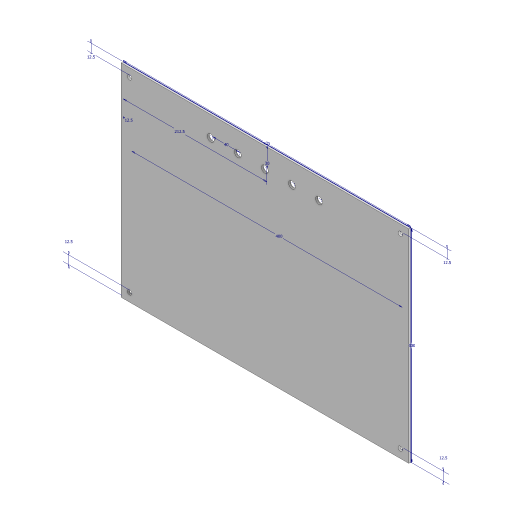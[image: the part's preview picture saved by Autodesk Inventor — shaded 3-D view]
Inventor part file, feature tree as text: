
AUTODESK INVENTOR PART (.ipt)
format: ipt  version: 2023 (Build 270158000, 158)  size: 107,520 bytes
history: native  units: mm
features: hole x2, sketch x1, extrude x1
ambient origin geometry x8: Origin, YZ Plane, XZ Plane, XY Plane, X Axis, Y Axis, Z Axis, Center Point
bodies: Solid1 (feature_tree)
feature tree (4):
  sketch  "Sketch1"  dims[d0=425.0mm d1=300.0mm d2=400.0mm d3=12.5mm d4=12.5mm d5=12.5mm d6=12.5mm d7=12.5mm d8=3.0mm d9=0.0mm d10=6.4mm d11=6.0mm d12=4.0mm d13=2.0mm d14=90.0deg d15=8.0mm d16=20.594885mm d17=50.0mm d19=40.0mm d20=10.0mm d22=10.0mm d24=212.5mm d25=10.0mm d26=6.0mm d27=4.0mm d28=2.0mm d29=90.0deg d30=8.0mm d31=20.594885mm d32=30.0mm]
  extrude  "Extrusion1"  Depth=300.0mm
  hole  "Hole1"  [1 undecoded]
  hole  "Hole2"  [1 undecoded]
note: 2 required parameter values undecoded (feature->parameter linkage not recoverable at this tier; creation-order binding heuristic only, values carry confidence <= 0.55)
